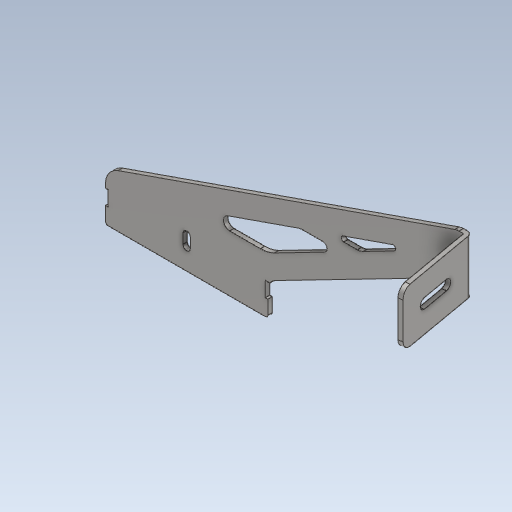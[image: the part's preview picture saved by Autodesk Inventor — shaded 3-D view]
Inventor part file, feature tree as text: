
AUTODESK INVENTOR PART (.ipt)
format: ipt  version: 2020 (Build 240168000, 168)  size: 206,848 bytes
history: native  units: mm
features: other x4, sketch x1, plane x1
ambient origin geometry x8: Origin, YZ Plane, XZ Plane, XY Plane, X Axis, Y Axis, Z Axis, Center Point
bodies: Body1 (feature_tree)
feature tree (6):
  other  "吊架-長(R)(#11.26).ipt"
  other  "實體1::吊架-長(R)(#11.26).ipt"
  other  "標籤特徵1"
  sketch  "草圖1"
  plane  "工作平面1"
  other  "實體1"
